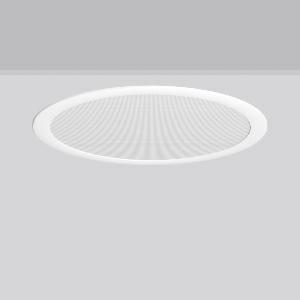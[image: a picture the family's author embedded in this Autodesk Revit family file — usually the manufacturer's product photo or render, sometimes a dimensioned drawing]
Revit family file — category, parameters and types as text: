
# Revit family: toledo_flat_round_e_901669_002_730_393b
name_source: partatom
category: Lighting Fixtures
units: mm (PartAtom-declared; Revit-internal decimal feet)

## family parameters
Cut with Voids When Loaded = No
Host = Face
Light Source = No
Part Type = Normal
Room Calculation Point = No
Round Connector Dimension = Use Diameter
Shared = No

## types (1)
- TuneableWhite 846 (1 x LED Modul 846, 2900 lm, 4600)
    Apparent Load = 30 VA
    CIE Flux Codes = 63 87 96 100 100
    Color Rendering = 80
    Color Temperature = 4600
    Default Elevation = 1800 mm
    Description = Series: TOLEDO FLAT round
Ultra thin recessed downlight. Housing: die-cast aluminium. Lightguide and diffuser made of non-yellowing PMMA, prismatic. Diffuser: transparent plastic, microprismatic. Tunable white dynamically adjustable from 2700 K to 6500 K.With Casambi smart+free Bluetooth control for wireless network and operation using Android / iOS devices, free app available for download. Ceiling installation with spring system. Mounting depth depends on ceiling strength. Including separate LED converter with connecting cable 250 mm. Suitable for through-wiring with separately available accessories. Surface mounted housing as accessory for all sizes. Retrofittable decorative cylinders made of chintz fabric as accessory, optional with satin finish plastic diffuser. Through-wiring box (5 pole) available as accessory. 
Colour: white
Diameter: 495 mm
Height: 6 mm
Cut-out diameter: 470 mm
Recess height: 55-75 mm
Luminaire: recess height: 31-51 mm
Lamp: LED
Socket: without socket
Colour temperature: 2700K - 6500K
Colour rendering index (CRI): 80
System power: 30 W
Rated luminous flux: 2900 lm
Luminous efficiency: 97 lm/W
System power 2: 31 W
Rated luminous flux 2: 2750 lm
Luminous efficiency 2: 89 lm/W
System power 3: 30 W
Rated luminous flux 3: 2800 lm
Luminous efficiency 3: 93 lm/W
Control gear: Dimmable Bluetooth converter
Protection class: II
Type of protection: IP 54
    Height = 0 mm  [stored 0 ft]
    Lamp = 1 x LED Modul 846
    Lamp Light Flux = 2900 lm
    Lamp count = 1
    Length = 495 mm
    Lifetime = 50000 h
    Luminous efficacy = 97 lm/W
    Manufacturer = RZB
    ModVariant = No
    Model = 901669.002.730
    Mounting Place = Ceiling
    Mounting Type = Recessed
    Number of Poles = 1
    OnlyDefault = Yes
    Power Factor = 1
    Product Name = TOLEDO FLAT round E
    Product group = Recessed downlights
    ProductGroupID = 402
    Protection Class = Protection class II
    Protection Degree = IP 20
    RLX_Detail_Level = 1
    RLX_Emergency_Light_Flux = 0 lm
    RLX_Emergency_Type = 0
    RLX_Emergency_Type_DB = No
    RlxData = <blob elided: 104833 chars, md5=4070980f>
    Socket = socket
    Standby Power = 0 W
    System Light Flux = 2900 lm
    System Power = 30 W
    Type Comments = TuneableWhite 846
    Type Image = 901586.002.jpg
    URL = http://relux.com
    VarID = tuneablewhite_846
    Voltage = 230 V
    Voltage Range = 220-240 V
    Weight = 0.00 kg
    Width = 0 mm  [stored 0 ft]

note: [stored X ft] marks values corroborated as IEEE doubles in the binary element streams (Revit-internal decimal feet)

## geometry (parser evidence)
native form markers: Blend x4, Sweep x10
no freeform markers — native parametric forms only
